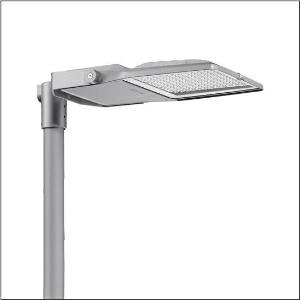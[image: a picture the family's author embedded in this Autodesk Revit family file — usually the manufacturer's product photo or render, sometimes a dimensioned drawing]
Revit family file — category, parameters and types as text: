
# Revit family: floodlight_fl_21_iq_midi___pl33t_5xa7781f4f3a_8e83
name_source: partatom
category: Lighting Fixtures
units: mm (PartAtom-declared; Revit-internal decimal feet)

## family parameters
Cut with Voids When Loaded = No
Host = Face
Light Source = No
Part Type = Normal
Room Calculation Point = No
Round Connector Dimension = Use Diameter
Shared = No

## types (1)
- --- (1 x LED, 36900 lm, 270.2 W, 4000K)
    Apparent Load = 270 VA
    CIE Flux Codes = 26 75 99 100 100
    Color Rendering = 70
    Color Temperature = 4000K
    Default Elevation = 1800 mm
    Description = Floodlight FL 21 iQ midi, floodlight, primary light control with lens, of PMMA, primary optical cover: protective disc, of toughened safety glass, transparent, light distribution: PL33T, light emission: direct distribution, installation type: surface-mounted, LED, High Power LED, rated luminous flux: 36.900lm, luminous efficacy: 137lm/W, light colour: 740, colour temperature: 4000K, control gear: ECG iQ, control: optimised constant luminous flux control (CLO 2.0), Desk-Remote (wireless, voltage-free reading and setting of iQ features in the workshop via application-optimized NFC function/RFID function), Light-Fading, Smart-Wire, Night-Set, Lumen-Switch, Temp-Guard, Auto-Match, with terminal, 6-pole, mains connection: 220..240V, AC, 50/60Hz, start of lifetime: 270W, end of service life: 287W, reduction: 118W, luminaire housing, of diecast aluminium, powder-coated, Siteco® metallic grey (DB 702S), corrosivity category C5 mid according to DIN EN ISO 12944, sealing non-destructively replaceable, please order mast flange separately, mast bracket, of steel, galvanised, powder-coated, Siteco® metallic grey (DB 702S), protection rating (complete): IP66, insulation class (complete): insulation class II (safety insulation), certification: CE, ENEC, VDE, protection symbol: D, impact resistance: IK08, permissible operating ambient temperature: -40..+40°C, permissible operating ambient temperature for outdoor applications: -40..+50°C, standard: DIN EN 12944, LABS conformity tested according to VDMA 24364:2018-05, packaging unit: 1 piece

Light Distribution: PL33T
    Height = 76 mm
    Lamp = 1 x LED
    Lamp Light Flux = 36900 lm
    Lamp Power = 270.2 W
    Lamp count = 1
    Length = 657 mm
    Luminous efficacy = 137 lm/W
    Manufacturer = Siteco
    ModVariant = No
    Model = 5XA7781F4F3A
    Number of Poles = 1
    OnlyDefault = Yes
    Power Factor = 1
    Product Name = Floodlight FL 21 iQ midi | PL33T
    Product group = floodlight | pylon annexe
    ProductGroupID = 6200
    Protection Class = Protection class II
    Protection Degree = IP 66
    RLX_Detail_Level = 1
    RLX_Emergency_Light_Flux = 0 lm
    RLX_Emergency_Type = 0
    RLX_Emergency_Type_DB = No
    RlxData = <blob elided: 153689 chars, md5=72bf026f>
    Socket = socket
    Standby Power = 0 W
    System Light Flux = 36900 lm
    System Power = 270 W
    Type Comments = factory setting: luminous flux: 100 % | dim-lin: 254 | 620 mA
    Type Image = l_1007123.jpg
    URL = http://relux.com
    VarID = @adj_072335
    Voltage = 0 V
    Weight = 0.00 kg
    Width = 442 mm

## geometry (parser evidence)
native form markers: Blend x4, Sweep x14
no freeform markers — native parametric forms only
